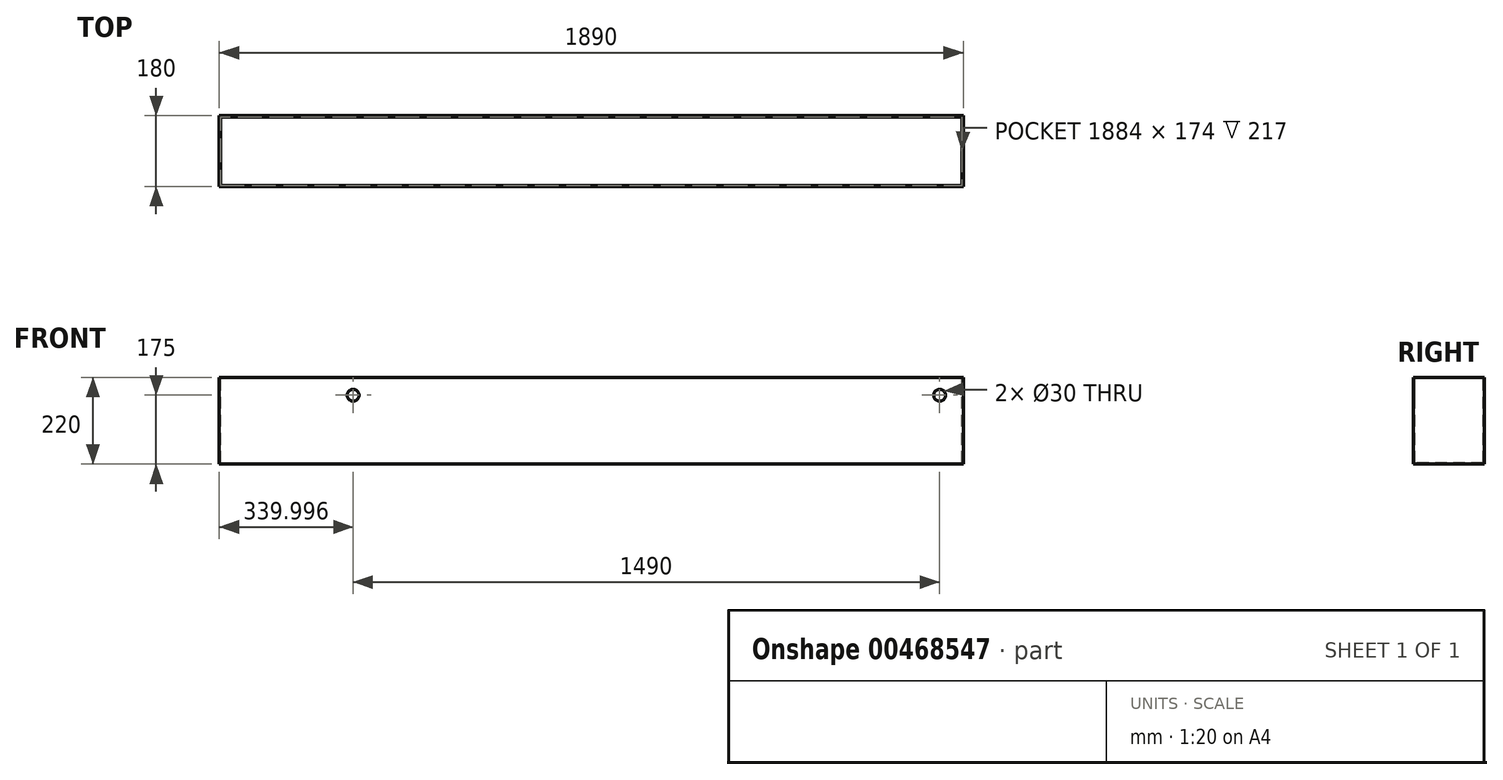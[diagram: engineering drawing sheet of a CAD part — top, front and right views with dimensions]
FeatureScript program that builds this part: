
annotation { "Feature Type Name" : "Feature", "Feature Type Description" : "" }
export const myFeature = defineFeature(function(context is Context, id is Id, definition is map)
    precondition{}
    {
        {
            var Q0;
            Q0=qCreatedBy(makeId("Top.planeOp"),FACE);
            var sketch = newSketch(context, id + "F0", { "sketchPlane" : qUnion([Q0])});
            skLineSegment(sketch, "E0.bottom", {"start": v(-46.21, 143.95) * mm, "end": v(1843.79, 143.95) * mm});
            skLineSegment(sketch, "E0.top", {"start": v(-46.21, -36.05) * mm, "end": v(1843.79, -36.05) * mm});
            skLineSegment(sketch, "E0.left", {"start": v(-46.21, 143.95) * mm, "end": v(-46.21, -36.05) * mm});
            skLineSegment(sketch, "E0.right", {"start": v(1843.79, 143.95) * mm, "end": v(1843.79, -36.05) * mm});
            skSolve(sketch);
        }
        {
            var Q0;
            Q0=makeQuery(id+"F0.imprint","IMPRINT",FACE,{"disambiguationData":[TD([[makeQuery(id+"F0.imprint","IMPRINT",EDGE,{"derivedFrom":sQuery(id+"F0.wireOp",EDGE,"E0.bottom")}),-1.0]])]});
            extrude(context, id + "F1", {"entities" : qUnion([Q0]), "depth" : 220 * mm, "offsetDistance" : 25 * mm});
        }
        {
            var Q0;
            Q0=makeQuery(id+"F1.opExtrude","CAP_FACE",FACE,{"disambiguationData":[OSD([sQuery(id+"F0.wireOp",EDGE,"E0.bottom"),sQuery(id+"F0.wireOp",EDGE,"E0.top"),sQuery(id+"F0.wireOp",EDGE,"E0.left"),sQuery(id+"F0.wireOp",EDGE,"E0.right")])],"isStart":false});
            var sketch = newSketch(context, id + "F2", { "sketchPlane" : qUnion([Q0])});
            skLineSegment(sketch, "E1.bottom", {"start": v(-43.21, 140.95) * mm, "end": v(1840.79, 140.95) * mm});
            skLineSegment(sketch, "E1.top", {"start": v(-43.21, -33.05) * mm, "end": v(1840.79, -33.05) * mm});
            skLineSegment(sketch, "E1.left", {"start": v(-43.21, 140.95) * mm, "end": v(-43.21, -33.05) * mm});
            skLineSegment(sketch, "E1.right", {"start": v(1840.79, 140.95) * mm, "end": v(1840.79, -33.05) * mm});
            skSolve(sketch);
        }
        {
            var Q0;
            Q0=qSketchRegion(id+"F2",true);
            extrude(context, id + "F3", {"entities" : qUnion([Q0]), "operationType" : NewBodyOperationType.REMOVE, "oppositeDirection" : true, "depth" : 217 * mm, "offsetDistance" : 25 * mm});
        }
        {
            var Q0;
            Q0=makeQuery(id+"F1.opExtrude","SWEPT_FACE",FACE,{"disambiguationData":[OSD([sQuery(id+"F0.wireOp",EDGE,"E0.top")])]});
            var sketch = newSketch(context, id + "F4", { "sketchPlane" : qUnion([Q0])});
            skLineSegment(sketch, "E2", {"start": v(1843.79, 175) * mm, "end": v(-46.21, 175) * mm, "construction": true});
            skCircle(sketch, "E3", {"center": v(293.79, 175) * mm, "radius": 15 * mm});
            skCircle(sketch, "E4", {"center": v(1783.79, 175) * mm, "radius": 15 * mm});
            skSolve(sketch);
        }
        {
            var Q0;
            Q0=makeQuery(id+"F4.imprint","IMPRINT",FACE,{"disambiguationData":[TD([[makeQuery(id+"F4.imprint","IMPRINT",EDGE,{"derivedFrom":sQuery(id+"F4.wireOp",EDGE,"E3")}),1.0]])]});
            var Q1;
            Q1=makeQuery(id+"F4.imprint","IMPRINT",FACE,{"disambiguationData":[TD([[makeQuery(id+"F4.imprint","IMPRINT",EDGE,{"derivedFrom":sQuery(id+"F4.wireOp",EDGE,"E4")}),1.0]])]});
            extrude(context, id + "F5", {"entities" : qUnion([Q0, Q1]), "operationType" : NewBodyOperationType.REMOVE, "endBound" : BoundingType.UP_TO_NEXT, "oppositeDirection" : true, "depth" : 25 * mm, "offsetDistance" : 25 * mm});
        }
    });
